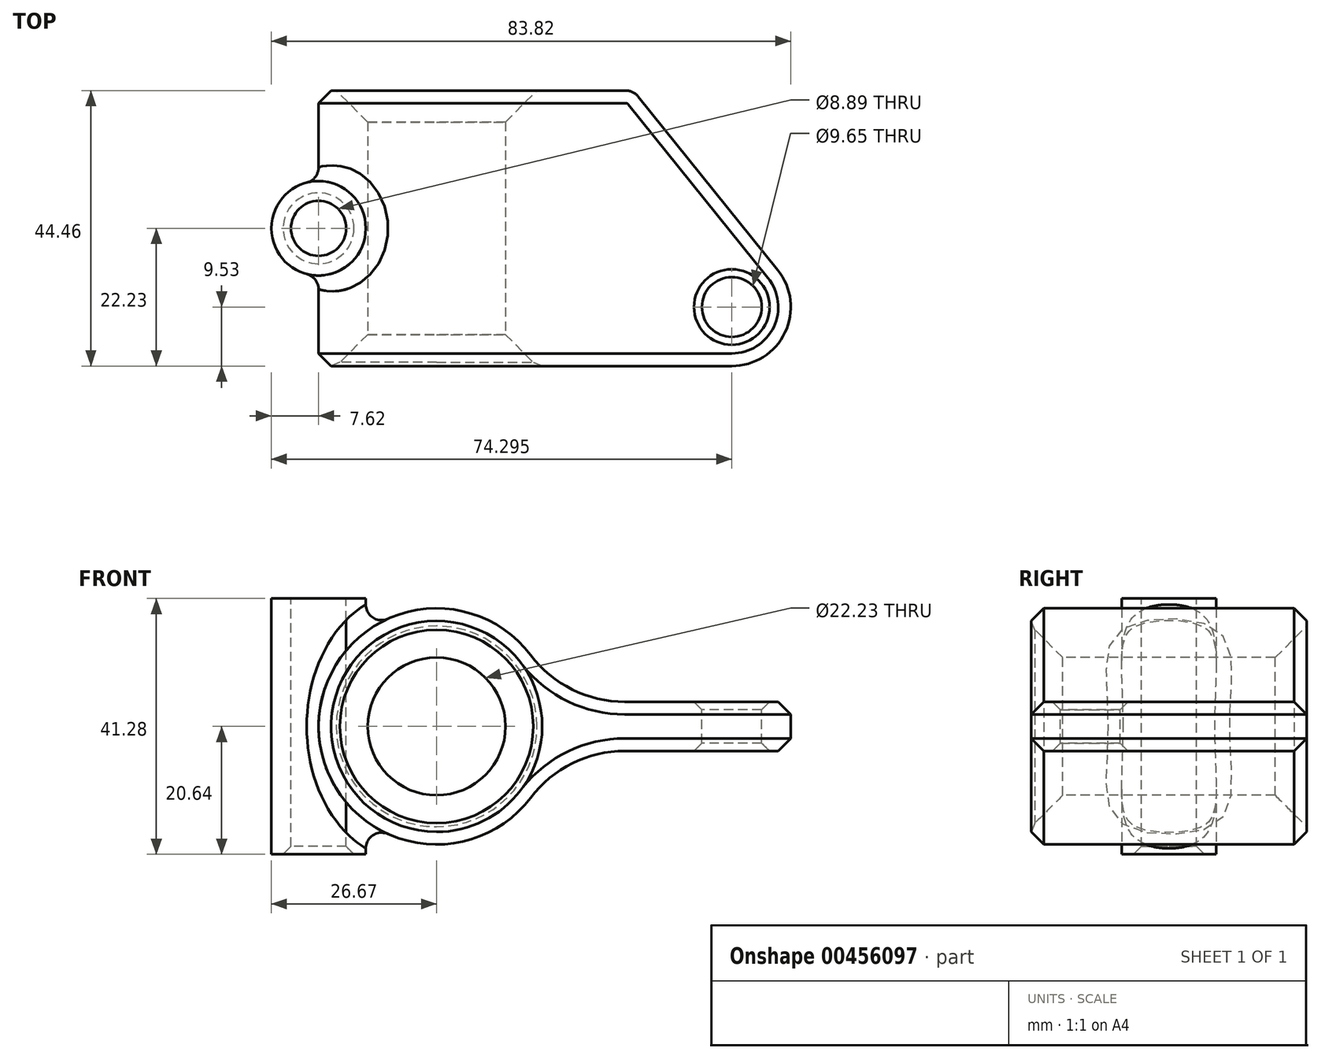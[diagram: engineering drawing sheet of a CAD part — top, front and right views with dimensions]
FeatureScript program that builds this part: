
annotation { "Feature Type Name" : "Feature", "Feature Type Description" : "" }
export const myFeature = defineFeature(function(context is Context, id is Id, definition is map)
    precondition{}
    {
        {
            var Q0;
            Q0=qCreatedBy(makeId("Front.planeOp"),FACE);
            var sketch = newSketch(context, id + "F0", { "sketchPlane" : qUnion([Q0])});
            skCircle(sketch, "E0", {"center": v(0, 0) * mm, "radius": 19.05 * mm});
            skSolve(sketch);
        }
        {
            var Q0;
            Q0=makeQuery(id+"F0.imprint","IMPRINT",FACE,{"disambiguationData":[TD([[makeQuery(id+"F0.imprint","IMPRINT",EDGE,{"derivedFrom":sQuery(id+"F0.wireOp",EDGE,"E0")}),1.0]])]});
            extrude(context, id + "F1", {"entities" : qUnion([Q0]), "depth" : 44.45 * mm, "symmetric" : true});
        }
        {
            var Q0;
            Q0=qCreatedBy(makeId("Top.planeOp"),FACE);
            var sketch = newSketch(context, id + "F2", { "sketchPlane" : qUnion([Q0])});
            skLineSegment(sketch, "E1.0", {"start": v(19.05, -22.23) * mm, "end": v(-19.05, -22.23) * mm});
            skLineSegment(sketch, "E1.1", {"start": v(19.05, 22.23) * mm, "end": v(-19.05, 22.23) * mm});
            skCircle(sketch, "E2", {"center": v(-19.05, 0) * mm, "radius": 7.62 * mm});
            skSolve(sketch);
        }
        {
            var Q0;
            Q0=makeQuery(id+"F2.imprint","IMPRINT",FACE,{"disambiguationData":[TD([[makeQuery(id+"F2.imprint","IMPRINT",EDGE,{"derivedFrom":sQuery(id+"F2.wireOp",EDGE,"E2")}),1.0]])]});
            extrude(context, id + "F3", {"entities" : qUnion([Q0]), "operationType" : NewBodyOperationType.ADD, "depth" : 41.27 * mm, "symmetric" : true});
        }
        {
            var Q0;
            Q0=qCreatedBy(makeId("Top.planeOp"),FACE);
            var sketch = newSketch(context, id + "F4", { "sketchPlane" : qUnion([Q0])});
            skLineSegment(sketch, "E3.0", {"start": v(19.05, 22.23) * mm, "end": v(-19.05, 22.23) * mm});
            skLineSegment(sketch, "E3.1", {"start": v(19.05, -22.23) * mm, "end": v(-19.05, -22.23) * mm});
            skLineSegment(sketch, "E4", {"start": v(0, -22.23) * mm, "end": v(0, 22.23) * mm});
            skLineSegment(sketch, "E5", {"start": v(0, 22.23) * mm, "end": v(31.75, 22.23) * mm});
            skLineSegment(sketch, "E6", {"start": v(31.75, 22.23) * mm, "end": v(55.05, -6.73) * mm});
            skLineSegment(sketch, "E7", {"start": v(19.05, -22.23) * mm, "end": v(47.63, -22.23) * mm});
            skArc(sketch, "E8", {"start": v(47.63, -22.23) * mm, "mid": v(56.22, -16.81) * mm, "end": v(55.05, -6.73) * mm});
            skSolve(sketch);
        }
        {
            var Q0;
            {var subQ3=sQuery(id+"F4.wireOp",EDGE,"E4");Q0=makeQuery(id+"F4.imprint","IMPRINT",FACE,{"disambiguationData":[TD([[makeQuery(id+"F4.imprint","IMPRINT",EDGE,{"derivedFrom":subQ3}),-1.0]])]});}
            extrude(context, id + "F5", {"entities" : qUnion([Q0]), "operationType" : NewBodyOperationType.ADD, "depth" : 7.94 * mm, "symmetric" : true});
        }
        {
            var Q0;
            Q0=makeQuery(id+"F3.opExtrude","CAP_FACE",FACE,{"disambiguationData":[OSD([sQuery(id+"F2.wireOp",EDGE,"E2")])],"isStart":false});
            var sketch = newSketch(context, id + "F6", { "sketchPlane" : qUnion([Q0])});
            skCircle(sketch, "E9.0", {"center": v(-19.05, 0) * mm, "radius": 4.44 * mm});
            skSolve(sketch);
        }
        {
            var Q0;
            Q0=makeQuery(id+"F6.imprint","IMPRINT",FACE,{"disambiguationData":[TD([[makeQuery(id+"F6.imprint","IMPRINT",EDGE,{"derivedFrom":sQuery(id+"F6.wireOp",EDGE,"E9.0")}),1.0]])]});
            extrude(context, id + "F7", {"entities" : qUnion([Q0]), "operationType" : NewBodyOperationType.REMOVE, "endBound" : BoundingType.THROUGH_ALL, "oppositeDirection" : true, "depth" : 25.4 * mm});
        }
        {
            var Q0;
            Q0=makeQuery(id+"F5.boolean.opBoolean","MERGE",FACE,{"derivedFrom":[makeQuery(id+"F1.opExtrude","CAP_FACE",FACE,{"disambiguationData":[OSD([sQuery(id+"F0.wireOp",EDGE,"E0")])],"isStart":false}),makeQuery(id+"F5.opExtrude","SWEPT_FACE",FACE,{"disambiguationData":[OSD([sQuery(id+"F4.wireOp",EDGE,"E3.1")])]})]});
            var sketch = newSketch(context, id + "F8", { "sketchPlane" : qUnion([Q0])});
            skCircle(sketch, "E10", {"center": v(0, 0) * mm, "radius": 11.11 * mm});
            skSolve(sketch);
        }
        {
            var Q0;
            Q0=makeQuery(id+"F8.imprint","IMPRINT",FACE,{"disambiguationData":[TD([[makeQuery(id+"F8.imprint","IMPRINT",EDGE,{"derivedFrom":sQuery(id+"F8.wireOp",EDGE,"E10")}),1.0]])]});
            extrude(context, id + "F9", {"entities" : qUnion([Q0]), "operationType" : NewBodyOperationType.REMOVE, "endBound" : BoundingType.THROUGH_ALL, "oppositeDirection" : true, "depth" : 25.4 * mm});
        }
        {
            var Q0;
            Q0=makeQuery(id+"F5.opExtrude","CAP_FACE",FACE,{"disambiguationData":[OSD([sQuery(id+"F4.wireOp",EDGE,"E3.1"),sQuery(id+"F4.wireOp",EDGE,"E4"),sQuery(id+"F4.wireOp",EDGE,"E5"),sQuery(id+"F4.wireOp",EDGE,"E6"),sQuery(id+"F4.wireOp",EDGE,"E8")])],"isStart":false});
            var sketch = newSketch(context, id + "F10", { "sketchPlane" : qUnion([Q0])});
            skCircle(sketch, "E11", {"center": v(47.63, -12.7) * mm, "radius": 4.83 * mm});
            skSolve(sketch);
        }
        {
            var Q0;
            Q0=makeQuery(id+"F10.imprint","IMPRINT",FACE,{"disambiguationData":[TD([[makeQuery(id+"F10.imprint","IMPRINT",EDGE,{"derivedFrom":sQuery(id+"F10.wireOp",EDGE,"E11")}),1.0]])]});
            extrude(context, id + "F11", {"entities" : qUnion([Q0]), "operationType" : NewBodyOperationType.ADD, "depth" : 25.4 * mm});
        }
        {
            var Q0;
            Q0=makeQuery(id+"F11.opExtrude","CAP_FACE",FACE,{"disambiguationData":[OSD([sQuery(id+"F10.wireOp",EDGE,"E11")])],"isStart":false});
            extrude(context, id + "F12", {"entities" : qUnion([Q0]), "operationType" : NewBodyOperationType.REMOVE, "endBound" : BoundingType.THROUGH_ALL, "oppositeDirection" : true, "depth" : 25.4 * mm});
        }
        {
            var Q0;
            Q0=makeQuery(id+"F5.boolean.opBoolean","INTERSECT",EDGE,{"derivedFrom":[makeQuery(id+"F1.opExtrude","SWEPT_FACE",FACE,{"disambiguationData":[OSD([sQuery(id+"F0.wireOp",EDGE,"E0")])]}),makeQuery(id+"F5.opExtrude","CAP_FACE",FACE,{"disambiguationData":[OSD([sQuery(id+"F4.wireOp",EDGE,"E3.1"),sQuery(id+"F4.wireOp",EDGE,"E4"),sQuery(id+"F4.wireOp",EDGE,"E5"),sQuery(id+"F4.wireOp",EDGE,"E6"),sQuery(id+"F4.wireOp",EDGE,"E8")])],"isStart":false})]});
            var Q1;
            Q1=makeQuery(id+"F5.boolean.opBoolean","INTERSECT",EDGE,{"derivedFrom":[makeQuery(id+"F1.opExtrude","SWEPT_FACE",FACE,{"disambiguationData":[OSD([sQuery(id+"F0.wireOp",EDGE,"E0")])]}),makeQuery(id+"F5.opExtrude","CAP_FACE",FACE,{"disambiguationData":[OSD([sQuery(id+"F4.wireOp",EDGE,"E3.1"),sQuery(id+"F4.wireOp",EDGE,"E4"),sQuery(id+"F4.wireOp",EDGE,"E5"),sQuery(id+"F4.wireOp",EDGE,"E6"),sQuery(id+"F4.wireOp",EDGE,"E8")])],"isStart":true})]});
            fillet(context, id + "F13", {"entities" : qUnion([Q0, Q1]), "radius" : 19.05 * mm, "tangentPropagation" : true, "allowEdgeOverflow" : false});
        }
        {
            var Q0;
            Q0=makeQuery(id+"F5.opExtrude","SWEPT_EDGE",EDGE,{"disambiguationData":[OSD([sQuery(id+"F4.wireOp",EDGE,"E5"),sQuery(id+"F4.wireOp",EDGE,"E6")])]});
            var Q1;
            Q1=makeQuery(id+"F3.boolean.opBoolean","INTERSECT",EDGE,{"derivedFrom":[makeQuery(id+"F1.opExtrude","SWEPT_FACE",FACE,{"disambiguationData":[OSD([sQuery(id+"F0.wireOp",EDGE,"E0")])]}),makeQuery(id+"F3.opExtrude","SWEPT_FACE",FACE,{"disambiguationData":[OSD([sQuery(id+"F2.wireOp",EDGE,"E2")])]})]});
            fillet(context, id + "F14", {"entities" : qUnion([Q0, Q1]), "radius" : 2.54 * mm, "tangentPropagation" : true, "allowEdgeOverflow" : false});
        }
        {
            var Q0;
            Q0=makeQuery(id+"F9.boolean.opBoolean","COPY",FACE,{"derivedFrom":makeQuery(id+"F9.opExtrude","SWEPT_FACE",FACE,{"disambiguationData":[OSD([sQuery(id+"F8.wireOp",EDGE,"E10")])]})});
            chamfer(context, id + "F15", {"entities" : qUnion([Q0]), "width" : 5.08 * mm, "tangentPropagation" : true});
        }
        {
            var Q0;
            Q0=makeQuery(id+"F7.boolean.opBoolean","INTERSECT",EDGE,{"derivedFrom":[makeQuery(id+"F3.opExtrude","CAP_FACE",FACE,{"disambiguationData":[OSD([sQuery(id+"F2.wireOp",EDGE,"E2")])],"isStart":true}),makeQuery(id+"F7.opExtrude","SWEPT_FACE",FACE,{"disambiguationData":[OSD([sQuery(id+"F6.wireOp",EDGE,"E9.0")])]})]});
            var Q1;
            Q1=makeQuery(id+"F7.boolean.opBoolean","COPY",EDGE,{"derivedFrom":makeQuery(id+"F7.opExtrude","CAP_EDGE",EDGE,{"disambiguationData":[OSD([sQuery(id+"F6.wireOp",EDGE,"E9.0")])],"isStart":true})});
            var Q2;
            Q2=makeQuery(id+"F12.boolean.opBoolean","COPY",FACE,{"derivedFrom":makeQuery(id+"F12.opExtrude","SWEPT_FACE",FACE,{"disambiguationData":[OSD([sQuery(id+"F10.wireOp",EDGE,"E11")])]})});
            chamfer(context, id + "F16", {"entities" : qUnion([Q0, Q1, Q2]), "width" : 1.27 * mm, "tangentPropagation" : true});
        }
        {
            var Q0;
            Q0=makeQuery(id+"F5.boolean.opBoolean","MERGE",FACE,{"derivedFrom":[makeQuery(id+"F1.opExtrude","CAP_FACE",FACE,{"disambiguationData":[OSD([sQuery(id+"F0.wireOp",EDGE,"E0")])],"isStart":false}),makeQuery(id+"F5.opExtrude","SWEPT_FACE",FACE,{"disambiguationData":[OSD([sQuery(id+"F4.wireOp",EDGE,"E3.1")])]})]});
            chamfer(context, id + "F17", {"entities" : qUnion([Q0]), "width" : 2.03 * mm, "tangentPropagation" : true});
        }
    });
